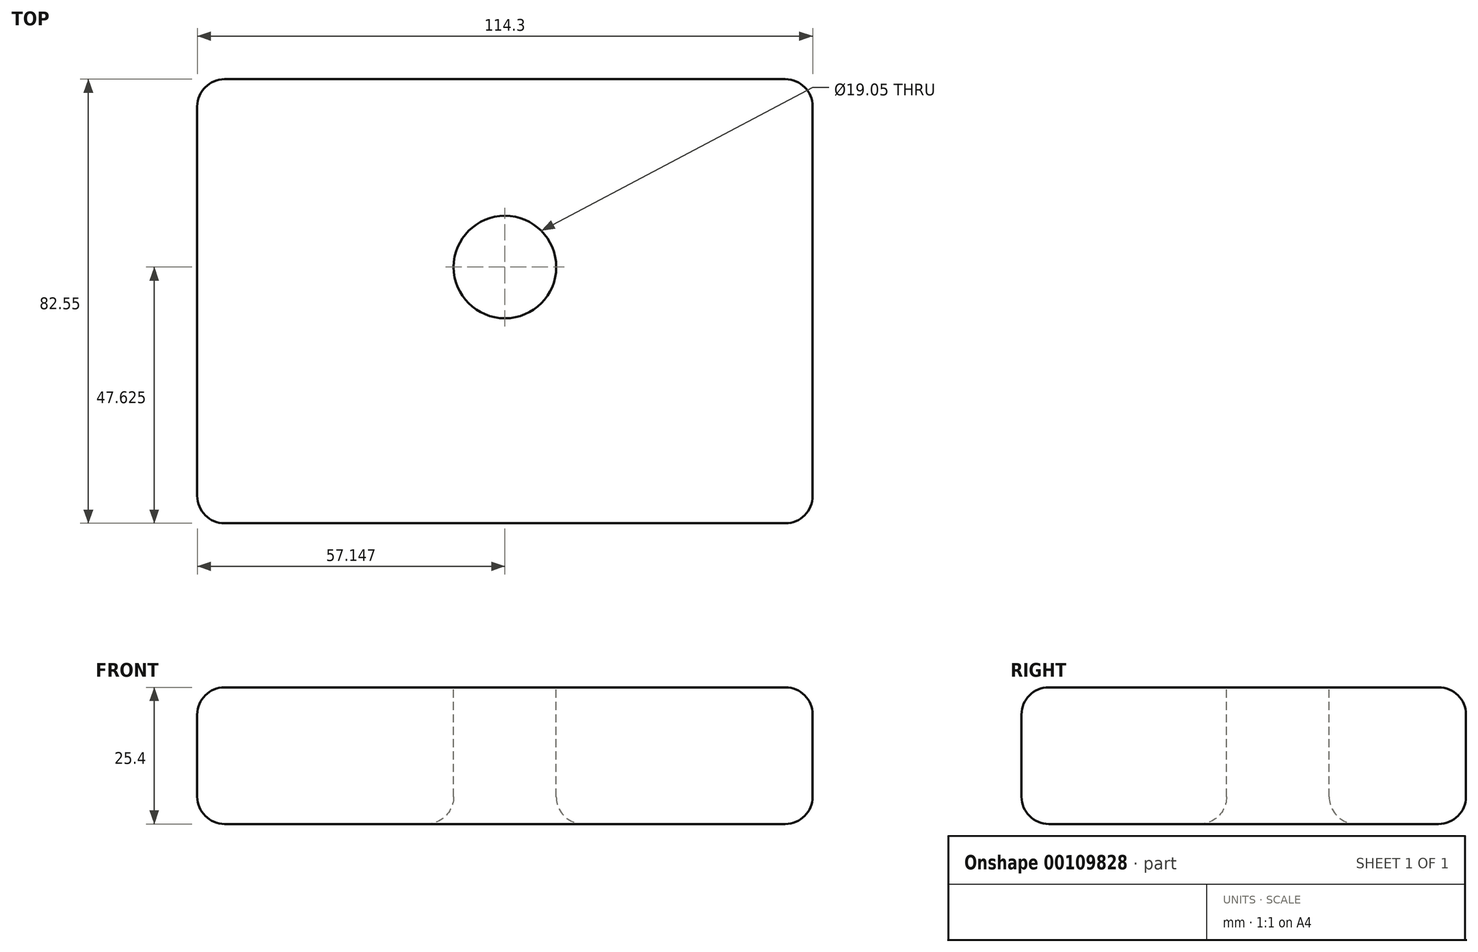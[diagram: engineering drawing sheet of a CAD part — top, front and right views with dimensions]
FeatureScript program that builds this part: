
annotation { "Feature Type Name" : "Feature", "Feature Type Description" : "" }
export const myFeature = defineFeature(function(context is Context, id is Id, definition is map)
    precondition{}
    {
        {
            var Q0;
            Q0=qCreatedBy(makeId("Top.planeOp"),FACE);
            var sketch = newSketch(context, id + "F0", { "sketchPlane" : qUnion([Q0])});
            skLineSegment(sketch, "E0.bottom", {"start": v(-70.36, 57.15) * mm, "end": v(43.94, 57.15) * mm});
            skLineSegment(sketch, "E0.top", {"start": v(-70.36, -25.4) * mm, "end": v(43.94, -25.4) * mm});
            skLineSegment(sketch, "E0.left", {"start": v(-70.36, 57.15) * mm, "end": v(-70.36, -25.4) * mm});
            skLineSegment(sketch, "E0.right", {"start": v(43.94, 57.15) * mm, "end": v(43.94, -25.4) * mm});
            skSolve(sketch);
        }
        {
            var Q0;
            Q0 = qSketchRegion(id + "F0", true);
            extrude(context, id + "F1", {"entities" : qUnion([Q0]), "depth" : 25.4 * mm});
        }
        {
            var Q0;
            Q0=makeQuery(id+"F1.opExtrude","CAP_FACE",FACE,{"disambiguationData":[OSD([sQuery(id+"F0.wireOp",EDGE,"E0.bottom"),sQuery(id+"F0.wireOp",EDGE,"E0.top"),sQuery(id+"F0.wireOp",EDGE,"E0.left"),sQuery(id+"F0.wireOp",EDGE,"E0.right")])],"isStart":false});
            var sketch = newSketch(context, id + "F2", { "sketchPlane" : qUnion([Q0])});
            skCircle(sketch, "E1", {"center": v(-13.21, 22.22) * mm, "radius": 9.53 * mm});
            skPoint(sketch, "E1.centerSnap0", {"position": v(-13.21, -25.4) * mm});
            skSolve(sketch);
        }
        {
            var Q0;
            Q0 = qSketchRegion(id + "F2", true);
            extrude(context, id + "F3", {"entities" : qUnion([Q0]), "operationType" : NewBodyOperationType.REMOVE, "oppositeDirection" : true, "depth" : 45.22 * mm});
        }
        {
            var Q0;
            Q0=makeQuery(id+"F1.opExtrude","SWEPT_EDGE",EDGE,{"disambiguationData":[OSD([sQuery(id+"F0.wireOp",EDGE,"E0.bottom"),sQuery(id+"F0.wireOp",EDGE,"E0.right")])]});
            var Q1;
            Q1=makeQuery(id+"F1.opExtrude","SWEPT_EDGE",EDGE,{"disambiguationData":[OSD([sQuery(id+"F0.wireOp",EDGE,"E0.bottom"),sQuery(id+"F0.wireOp",EDGE,"E0.left")])]});
            var Q2;
            Q2=makeQuery(id+"F1.opExtrude","SWEPT_EDGE",EDGE,{"disambiguationData":[OSD([sQuery(id+"F0.wireOp",EDGE,"E0.top"),sQuery(id+"F0.wireOp",EDGE,"E0.right")])]});
            var Q3;
            Q3=makeQuery(id+"F1.opExtrude","SWEPT_EDGE",EDGE,{"disambiguationData":[OSD([sQuery(id+"F0.wireOp",EDGE,"E0.top"),sQuery(id+"F0.wireOp",EDGE,"E0.left")])]});
            var Q4;
            Q4=makeQuery(id+"F1.opExtrude","CAP_EDGE",EDGE,{"disambiguationData":[OSD([sQuery(id+"F0.wireOp",EDGE,"E0.top")])],"isStart":false});
            var Q5;
            Q5=makeQuery(id+"F1.opExtrude","CAP_EDGE",EDGE,{"disambiguationData":[OSD([sQuery(id+"F0.wireOp",EDGE,"E0.left")])],"isStart":false});
            var Q6;
            Q6=makeQuery(id+"F1.opExtrude","CAP_EDGE",EDGE,{"disambiguationData":[OSD([sQuery(id+"F0.wireOp",EDGE,"E0.left")])],"isStart":true});
            var Q7;
            Q7=makeQuery(id+"F1.opExtrude","CAP_FACE",FACE,{"disambiguationData":[OSD([sQuery(id+"F0.wireOp",EDGE,"E0.bottom"),sQuery(id+"F0.wireOp",EDGE,"E0.top"),sQuery(id+"F0.wireOp",EDGE,"E0.left"),sQuery(id+"F0.wireOp",EDGE,"E0.right")])],"isStart":true});
            fillet(context, id + "F4", {"entities" : qUnion([Q0, Q1, Q2, Q3, Q4, Q5, Q6, Q7]), "radius" : 5.08 * mm, "tangentPropagation" : true, "allowEdgeOverflow" : false});
        }
        {
            var Q0;
            Q0=makeQuery(id+"F1.opExtrude","CAP_EDGE",EDGE,{"disambiguationData":[OSD([sQuery(id+"F0.wireOp",EDGE,"E0.bottom")])],"isStart":false});
            var Q1;
            Q1=makeQuery(id+"F3.boolean.opBoolean","COPY",EDGE,{"derivedFrom":makeQuery(id+"F3.opExtrude","CAP_EDGE",EDGE,{"disambiguationData":[OSD([sQuery(id+"F2.wireOp",EDGE,"E1")])],"isStart":true})});
            fillet(context, id + "F5", {"entities" : qUnion([Q0, Q1]), "radius" : 5.08 * mm, "tangentPropagation" : true, "allowEdgeOverflow" : false});
        }
    });
